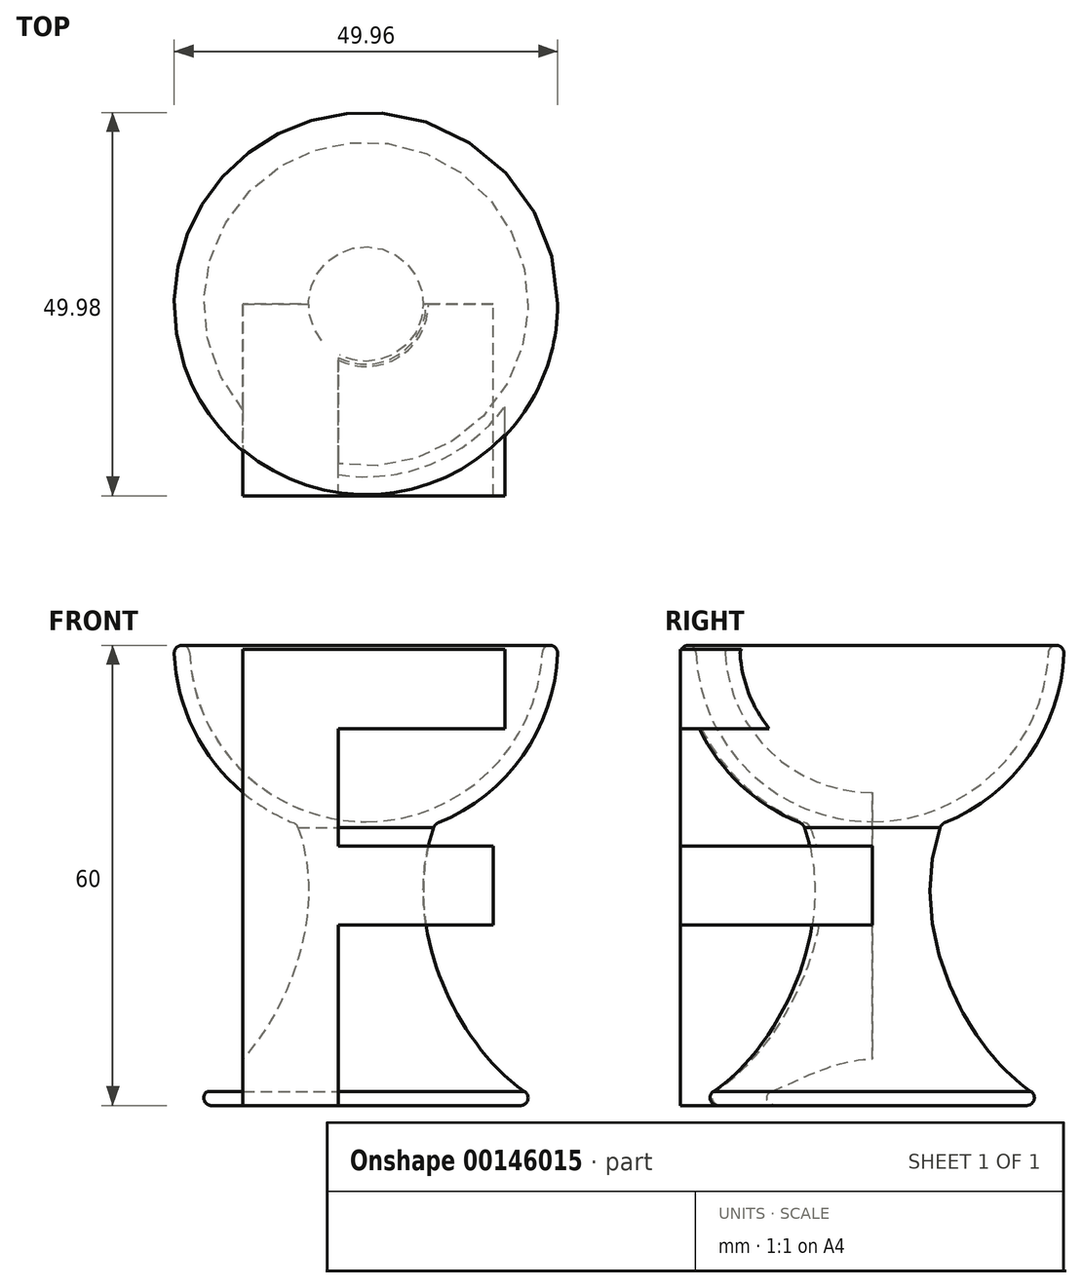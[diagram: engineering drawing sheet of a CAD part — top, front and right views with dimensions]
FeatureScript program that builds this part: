
annotation { "Feature Type Name" : "Feature", "Feature Type Description" : "" }
export const myFeature = defineFeature(function(context is Context, id is Id, definition is map)
    precondition{}
    {
        {
            var Q0;
            Q0=qCreatedBy(makeId("Top.planeOp"),FACE);
            var sketch = newSketch(context, id + "F0", { "sketchPlane" : qUnion([Q0])});
            skCircle(sketch, "E0", {"center": v(0, 0) * mm, "radius": 25 * mm});
            skSolve(sketch);
        }
        {
            var Q0;
            Q0 = qSketchRegion(id + "F0", true);
            extrude(context, id + "F1", {"entities" : qUnion([Q0]), "depth" : 60 * mm});
        }
        {
            var Q0;
            Q0=qCreatedBy(makeId("Front.planeOp"),FACE);
            var sketch = newSketch(context, id + "F2", { "sketchPlane" : qUnion([Q0])});
            skLineSegment(sketch, "E1", {"start": v(-25, -23.08) * mm, "end": v(-25, 71.14) * mm, "construction": true});
            skArc(sketch, "E2", {"start": v(-25, 60) * mm, "mid": v(-20.62, 45.86) * mm, "end": v(-9, 36.68) * mm});
            skLineSegment(sketch, "E3", {"start": v(-48.76, 60) * mm, "end": v(50.95, 60) * mm, "construction": true});
            skPoint(sketch, "E3.startSnap0", {"position": v(-25, 60) * mm});
            skFitSpline(sketch, "E4", {"points": [v(-9, 36.68) * mm, v(-25, 0) * mm, v(-42.72, 20.31) * mm], "startDerivative": vector(32.9, -88.21) * mm, "endDerivative": vector(-41.6, 70.27) * mm});
            skPoint(sketch, "E5.orphan", {"position": v(0, 35) * mm});
            skPoint(sketch, "E6.orphan", {"position": v(0, 85) * mm});
            skLineSegment(sketch, "E7", {"start": v(-25, 60) * mm, "end": v(-25, 0) * mm});
            skLineSegment(sketch, "E8", {"start": v(0, 71.24) * mm, "end": v(0, -21.82) * mm, "construction": true});
            skSolve(sketch);
        }
        {
            var Q0;
            Q0 = qSketchRegion(id + "F2", true);
            var Q1;
            Q1=sQuery(id+"F2.wireOp",EDGE,"E8");
            revolve(context, id + "F3", {"operationType" : NewBodyOperationType.REMOVE, "entities" : qUnion([Q0]), "axis" : qUnion([Q1]), "revolveType" : RevolveType.FULL, "oppositeDirection" : true});
        }
        {
            var Q0;
            Q0=qCreatedBy(makeId("Front.planeOp"),FACE);
            var sketch = newSketch(context, id + "F4", { "sketchPlane" : qUnion([Q0])});
            skText(sketch, "E9", { "text": "F", "fontName": "OpenSans-Bold.ttf"});
            const initialGuessF4  = {"E9": [-0.0235, 0, 1, 0, 0.06]};
            skSetInitialGuess(sketch, initialGuessF4);
            skSolve(sketch);
        }
        {
            var Q0;
            Q0 = qSketchRegion(id + "F4", true);
            extrude(context, id + "F5", {"entities" : qUnion([Q0]), "operationType" : NewBodyOperationType.ADD, "depth" : 25 * mm});
        }
        {
            var Q0;
            Q0=qCreatedBy(makeId("Front.planeOp"),FACE);
            var sketch = newSketch(context, id + "F6", { "sketchPlane" : qUnion([Q0])});
            skArc(sketch, "E10", {"start": v(0, 37) * mm, "mid": v(23, 60) * mm, "end": v(0, 83) * mm});
            skLineSegment(sketch, "E11", {"start": v(0, 83) * mm, "end": v(0, 37) * mm});
            skSolve(sketch);
        }
        {
            var Q0;
            Q0=makeQuery(id+"F6.imprint","IMPRINT",FACE,{"disambiguationData":[TD([[makeQuery(id+"F6.imprint","IMPRINT",EDGE,{"derivedFrom":sQuery(id+"F6.wireOp",EDGE,"E10")}),1.0]])]});
            var Q1;
            Q1=sQuery(id+"F6.wireOp",EDGE,"E11");
            revolve(context, id + "F7", {"operationType" : NewBodyOperationType.REMOVE, "entities" : qUnion([Q0]), "axis" : qUnion([Q1]), "revolveType" : RevolveType.FULL, "oppositeDirection" : true});
        }
        {
            var Q0;
            Q0=makeQuery(id+"F3.boolean.opBoolean","MERGE",EDGE,{"derivedFrom":[makeQuery(id+"F1.opExtrude","CAP_EDGE",EDGE,{"disambiguationData":[OSD([sQuery(id+"F0.wireOp",EDGE,"E0")])],"isStart":false}),makeQuery(id+"F3.opRevolve","SWEPT_EDGE",EDGE,{"disambiguationData":[OSD([sQuery(id+"F2.wireOp",EDGE,"E2"),sQuery(id+"F2.wireOp",EDGE,"E7")])]})]});
            var Q1;
            Q1=makeQuery(id+"F7.boolean.opBoolean","INTERSECT",EDGE,{"derivedFrom":[makeQuery(id+"F1.opExtrude","CAP_FACE",FACE,{"disambiguationData":[OSD([sQuery(id+"F0.wireOp",EDGE,"E0")])],"isStart":false}),makeQuery(id+"F7.opRevolve","SWEPT_FACE",FACE,{"disambiguationData":[OSD([sQuery(id+"F6.wireOp",EDGE,"E10")])]})]});
            var Q2;
            Q2=makeQuery(id+"F3.boolean.opBoolean","COPY",EDGE,{"derivedFrom":makeQuery(id+"F3.opRevolve","SWEPT_EDGE",EDGE,{"disambiguationData":[OSD([sQuery(id+"F2.wireOp",EDGE,"E2"),sQuery(id+"F2.wireOp",EDGE,"E4")])]})});
            var Q3;
            Q3=makeQuery(id+"F3.boolean.opBoolean","MERGE",EDGE,{"derivedFrom":[makeQuery(id+"F1.opExtrude","CAP_EDGE",EDGE,{"disambiguationData":[OSD([sQuery(id+"F0.wireOp",EDGE,"E0")])],"isStart":true}),makeQuery(id+"F3.opRevolve","SWEPT_EDGE",EDGE,{"disambiguationData":[OSD([sQuery(id+"F2.wireOp",EDGE,"E4"),sQuery(id+"F2.wireOp",EDGE,"E7")])]})]});
            fillet(context, id + "F8", {"entities" : qUnion([Q0, Q1, Q2, Q3]), "radius" : 1 * mm, "tangentPropagation" : true, "allowEdgeOverflow" : false});
        }
    });
